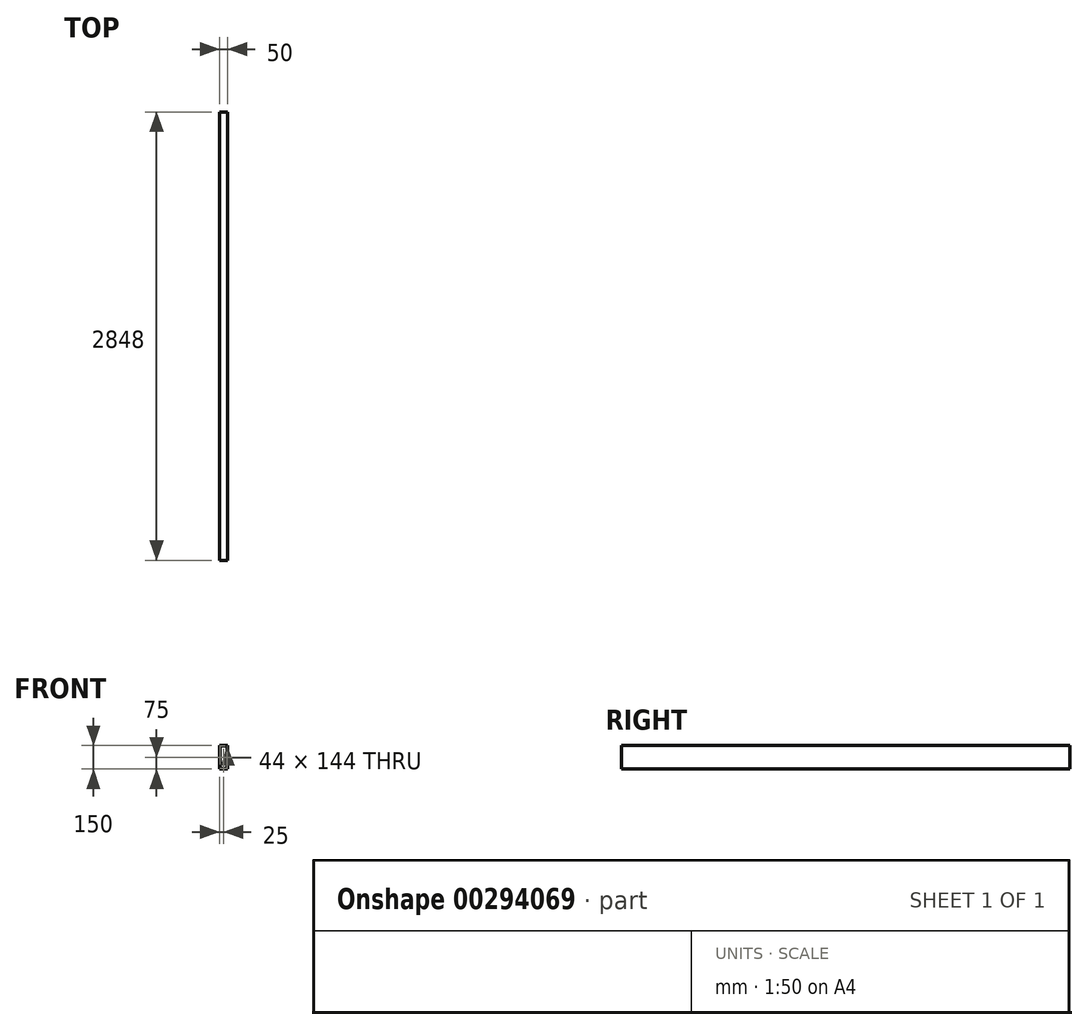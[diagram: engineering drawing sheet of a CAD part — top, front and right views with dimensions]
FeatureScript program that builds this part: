
annotation { "Feature Type Name" : "Feature", "Feature Type Description" : "" }
export const myFeature = defineFeature(function(context is Context, id is Id, definition is map)
    precondition{}
    {
        {
            var Q0;
            Q0=qCreatedBy(makeId("Front.planeOp"),FACE);
            var sketch = newSketch(context, id + "F0", { "sketchPlane" : qUnion([Q0])});
            skLineSegment(sketch, "E0", {"start": v(0, 0) * mm, "end": v(50, 0) * mm});
            skLineSegment(sketch, "E1", {"start": v(50, 0) * mm, "end": v(50, 150) * mm});
            skLineSegment(sketch, "E2", {"start": v(0, 150) * mm, "end": v(0, 0) * mm});
            skLineSegment(sketch, "E3", {"start": v(0, 150) * mm, "end": v(50, 150) * mm});
            skLineSegment(sketch, "E4.bottom", {"start": v(3, 147) * mm, "end": v(47, 147) * mm});
            skLineSegment(sketch, "E4.top", {"start": v(3, 3) * mm, "end": v(47, 3) * mm});
            skLineSegment(sketch, "E4.left", {"start": v(3, 147) * mm, "end": v(3, 3) * mm});
            skLineSegment(sketch, "E4.right", {"start": v(47, 147) * mm, "end": v(47, 3) * mm});
            skSolve(sketch);
        }
        {
            var Q0;
            Q0=makeQuery(id+"F0.imprint","IMPRINT",FACE,{"disambiguationData":[TD([[makeQuery(id+"F0.imprint","IMPRINT",EDGE,{"derivedFrom":sQuery(id+"F0.wireOp",EDGE,"E0")}),1.0]])]});
            extrude(context, id + "F1", {"entities" : qUnion([Q0]), "depth" : 2848 * mm});
        }
    });
